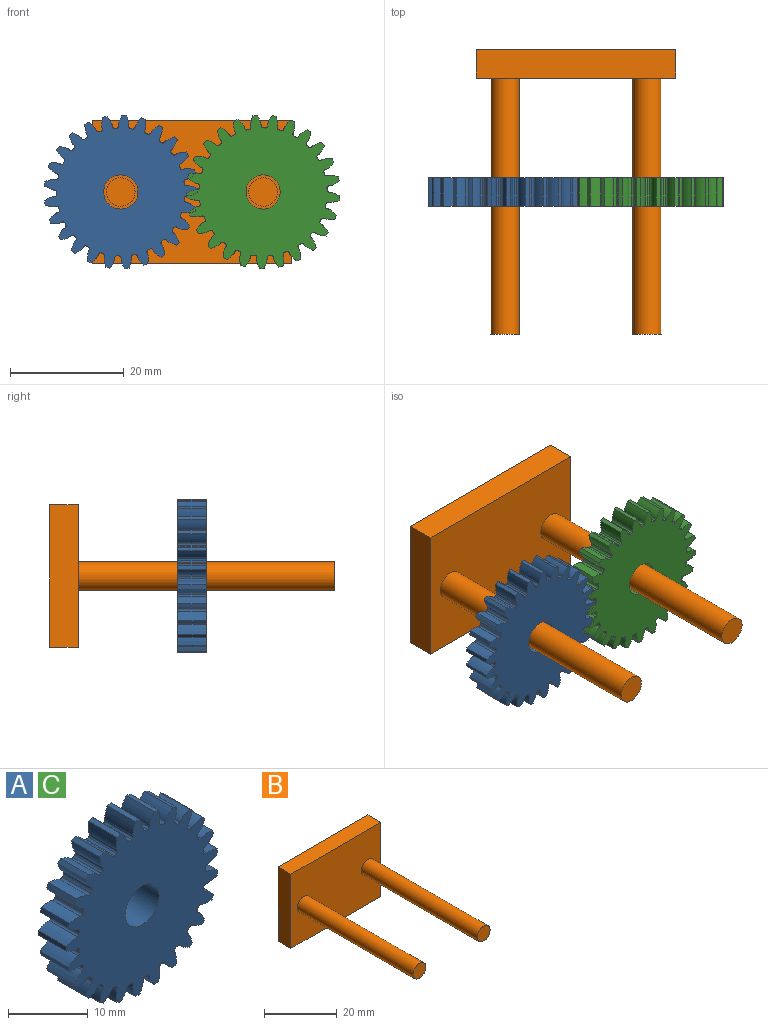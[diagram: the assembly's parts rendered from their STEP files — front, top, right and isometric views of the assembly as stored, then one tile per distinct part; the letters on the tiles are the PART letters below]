
ASSEMBLY  parts=3 mates=2
PART A: 153 faces, bbox 26.9x5x27 mm
  f0: extruded ~5x1.84mm, area 10.1mm2, adj f100,f101,f102,f103
  f1: cylinder r=11.25mm len=5mm, axis (0,1,0), area 1.9mm2, adj f101,f102,f103,f104
  f2: extruded ~5x1.84mm, area 10.1mm2, adj f3,f101,f102,f104
  f3: cylinder r=13.5mm len=5mm, axis (0,1,0), area 3.6mm2, adj f2,f4,f101,f102
  f4: extruded ~5x1.98mm, area 10.1mm2, adj f3,f101,f102,f105
  f5: cylinder r=11.25mm len=5mm, axis (0,1,0), area 1.9mm2, adj f101,f102,f105,f106
  f6: extruded ~5x1.59mm, area 10.1mm2, adj f7,f101,f102,f106
  f7: cylinder r=13.5mm len=5mm, axis (0,1,0), area 3.6mm2, adj f6,f8,f101,f102
  f8: extruded ~5x1.99mm, area 10.1mm2, adj f7,f101,f102,f107
  f9: cylinder r=11.25mm len=5mm, axis (0,1,0), area 1.9mm2, adj f101,f102,f107,f108
  f10: extruded ~5x1.57mm, area 10.1mm2, adj f11,f101,f102,f108
  f11: cylinder r=13.5mm len=5mm, axis (0,1,0), area 3.6mm2, adj f10,f12,f101,f102
  f12: extruded ~5x1.88mm, area 10.1mm2, adj f11,f101,f102,f109
  f13: cylinder r=11.25mm len=5mm, axis (0,1,0), area 1.9mm2, adj f101,f102,f109,f110
  f14: extruded ~5x1.83mm, area 10.1mm2, adj f15,f101,f102,f110
  f15: cylinder r=13.5mm len=5mm, axis (0,1,0), area 3.6mm2, adj f14,f16,f101,f102
  f16: extruded ~5x1.65mm, area 10.1mm2, adj f15,f101,f102,f111
  f17: cylinder r=11.25mm len=5mm, axis (0,1,0), area 1.9mm2, adj f101,f102,f111,f112
  f18: extruded ~5x1.97mm, area 10.1mm2, adj f19,f101,f102,f112
  f19: cylinder r=13.5mm len=5mm, axis (0,1,0), area 3.6mm2, adj f18,f20,f101,f102
  f20: extruded ~5x1.51mm, area 10.1mm2, adj f19,f101,f102,f113
  f21: cylinder r=11.25mm len=5mm, axis (0,1,0), area 1.9mm2, adj f101,f102,f113,f114
  f22: extruded ~5x1.99mm, area 10.1mm2, adj f23,f101,f102,f114
  f23: cylinder r=13.5mm len=5mm, axis (0,1,0), area 3.6mm2, adj f22,f24,f101,f102
  f24: extruded ~5x1.79mm, area 10.1mm2, adj f23,f101,f102,f115
  f25: cylinder r=11.25mm len=5mm, axis (0,1,0), area 1.9mm2, adj f101,f102,f115,f116
  f26: extruded ~5x1.89mm, area 10.1mm2, adj f27,f101,f102,f116
  f27: cylinder r=13.5mm len=5mm, axis (0,1,0), area 3.6mm2, adj f26,f28,f101,f102
  f28: extruded ~5x1.96mm, area 10.1mm2, adj f27,f101,f102,f117
  f29: cylinder r=11.25mm len=5mm, axis (0,1,0), area 1.9mm2, adj f101,f102,f117,f118
  f30: extruded ~5x1.67mm, area 10.1mm2, adj f31,f101,f102,f118
  f31: cylinder r=13.5mm len=5mm, axis (0,1,0), area 3.6mm2, adj f30,f32,f101,f102
  f32: extruded ~5x2mm, area 10.1mm2, adj f31,f101,f102,f119
  f33: cylinder r=11.25mm len=5mm, axis (0,1,0), area 1.9mm2, adj f101,f102,f119,f120
  f34: extruded ~5x1.49mm, area 10.1mm2, adj f35,f101,f102,f120
  f35: cylinder r=13.5mm len=5mm, axis (0,1,0), area 3.6mm2, adj f34,f36,f101,f102
  f36: extruded ~5x1.92mm, area 10.1mm2, adj f35,f101,f102,f121
  f37: cylinder r=11.25mm len=5mm, axis (0,1,0), area 1.9mm2, adj f101,f102,f121,f122
  f38: extruded ~5x1.78mm, area 10.1mm2, adj f39,f101,f102,f122
  f39: cylinder r=13.5mm len=5mm, axis (0,1,0), area 3.6mm2, adj f38,f40,f101,f102
  f40: extruded ~5x1.72mm, area 10.1mm2, adj f39,f101,f102,f123
  f41: cylinder r=11.25mm len=5mm, axis (0,1,0), area 1.9mm2, adj f101,f102,f123,f124
  f42: extruded ~5x1.95mm, area 10.1mm2, adj f43,f101,f102,f124
  f43: cylinder r=13.5mm len=5mm, axis (0,1,0), area 3.6mm2, adj f42,f44,f101,f102
  f44: extruded ~5x1.43mm, area 10.1mm2, adj f43,f101,f102,f125
  f45: cylinder r=11.25mm len=5mm, axis (0,1,0), area 1.9mm2, adj f101,f102,f125,f126
  f46: extruded ~5x2mm, area 10.1mm2, adj f47,f101,f102,f126
  f47: cylinder r=13.5mm len=5mm, axis (0,1,0), area 3.6mm2, adj f46,f48,f101,f102
  f48: extruded ~5x1.73mm, area 10.1mm2, adj f47,f101,f102,f127
  f49: cylinder r=11.25mm len=5mm, axis (0,1,0), area 1.9mm2, adj f101,f102,f127,f128
  f50: extruded ~5x1.93mm, area 10.1mm2, adj f51,f101,f102,f128
  f51: cylinder r=13.5mm len=5mm, axis (0,1,0), area 3.6mm2, adj f50,f52,f101,f102
  f52: extruded ~5x1.93mm, area 10.1mm2, adj f51,f101,f102,f129
  f53: cylinder r=11.25mm len=5mm, axis (0,1,0), area 1.9mm2, adj f101,f102,f129,f130
  f54: extruded ~5x1.73mm, area 10.1mm2, adj f55,f101,f102,f130
  f55: cylinder r=13.5mm len=5mm, axis (0,1,0), area 3.6mm2, adj f54,f56,f101,f102
  f56: extruded ~5x2mm, area 10.1mm2, adj f55,f101,f102,f131
  f57: cylinder r=11.25mm len=5mm, axis (0,1,0), area 1.9mm2, adj f101,f102,f131,f132
  f58: extruded ~5x1.43mm, area 10.1mm2, adj f59,f101,f102,f132
  f59: cylinder r=13.5mm len=5mm, axis (0,1,0), area 3.6mm2, adj f58,f60,f101,f102
  f60: extruded ~5x1.95mm, area 10.1mm2, adj f59,f101,f102,f133
  f61: cylinder r=11.25mm len=5mm, axis (0,1,0), area 1.9mm2, adj f101,f102,f133,f134
  f62: extruded ~5x1.72mm, area 10.1mm2, adj f63,f101,f102,f134
  f63: cylinder r=13.5mm len=5mm, axis (0,1,0), area 3.6mm2, adj f62,f64,f101,f102
  f64: extruded ~5x1.78mm, area 10.1mm2, adj f63,f101,f102,f135
  f65: cylinder r=11.25mm len=5mm, axis (0,1,0), area 1.9mm2, adj f101,f102,f135,f136
  f66: extruded ~5x1.92mm, area 10.1mm2, adj f67,f101,f102,f136
  f67: cylinder r=13.5mm len=5mm, axis (0,1,0), area 3.6mm2, adj f66,f68,f101,f102
  f68: extruded ~5x1.49mm, area 10.1mm2, adj f67,f101,f102,f137
  f69: cylinder r=11.25mm len=5mm, axis (0,1,0), area 1.9mm2, adj f101,f102,f137,f138
  f70: extruded ~5x2mm, area 10.1mm2, adj f71,f101,f102,f138
  f71: cylinder r=13.5mm len=5mm, axis (0,1,0), area 3.6mm2, adj f70,f72,f101,f102
  f72: extruded ~5x1.67mm, area 10.1mm2, adj f71,f101,f102,f139
  f73: cylinder r=11.25mm len=5mm, axis (0,1,0), area 1.9mm2, adj f101,f102,f139,f140
  f74: extruded ~5x1.96mm, area 10.1mm2, adj f75,f101,f102,f140
  f75: cylinder r=13.5mm len=5mm, axis (0,1,0), area 3.6mm2, adj f74,f76,f101,f102
  f76: extruded ~5x1.89mm, area 10.1mm2, adj f75,f101,f102,f141
  f77: cylinder r=11.25mm len=5mm, axis (0,1,0), area 1.9mm2, adj f101,f102,f141,f142
  f78: extruded ~5x1.79mm, area 10.1mm2, adj f79,f101,f102,f142
  f79: cylinder r=13.5mm len=5mm, axis (0,1,0), area 3.6mm2, adj f78,f80,f101,f102
  f80: extruded ~5x1.99mm, area 10.1mm2, adj f79,f101,f102,f143
  f81: cylinder r=11.25mm len=5mm, axis (0,1,0), area 1.9mm2, adj f101,f102,f143,f144
  f82: extruded ~5x1.51mm, area 10.1mm2, adj f83,f101,f102,f144
  f83: cylinder r=13.5mm len=5mm, axis (0,1,0), area 3.6mm2, adj f82,f84,f101,f102
  f84: extruded ~5x1.97mm, area 10.1mm2, adj f83,f101,f102,f145
  f85: cylinder r=11.25mm len=5mm, axis (0,1,0), area 1.9mm2, adj f101,f102,f145,f146
  f86: extruded ~5x1.65mm, area 10.1mm2, adj f87,f101,f102,f146
  f87: cylinder r=13.5mm len=5mm, axis (0,1,0), area 3.6mm2, adj f86,f88,f101,f102
  f88: extruded ~5x1.83mm, area 10.1mm2, adj f87,f101,f102,f147
  f89: cylinder r=11.25mm len=5mm, axis (0,1,0), area 1.9mm2, adj f101,f102,f147,f148
  f90: extruded ~5x1.88mm, area 10.1mm2, adj f91,f101,f102,f148
  f91: cylinder r=13.5mm len=5mm, axis (0,1,0), area 3.6mm2, adj f90,f92,f101,f102
  f92: extruded ~5x1.57mm, area 10.1mm2, adj f91,f101,f102,f149
  f93: cylinder r=11.25mm len=5mm, axis (0,1,0), area 1.9mm2, adj f101,f102,f149,f150
  f94: extruded ~5x1.99mm, area 10.1mm2, adj f95,f101,f102,f150
  f95: cylinder r=13.5mm len=5mm, axis (0,1,0), area 3.6mm2, adj f94,f96,f101,f102
  f96: extruded ~5x1.59mm, area 10.1mm2, adj f95,f101,f102,f151
  f97: cylinder r=11.25mm len=5mm, axis (0,1,0), area 1.9mm2, adj f101,f102,f151,f152
  f98: extruded ~5x1.98mm, area 10.1mm2, adj f100,f101,f102,f152
  f99: cylinder r=3mm len=6mm, axis (0,1,0), area 94.2mm2, adj f101,f102
  f100: cylinder r=13.5mm len=5mm, axis (0,1,0), area 3.6mm2, adj f0,f98,f101,f102
  f101: plane 26.99x26.94mm, normal (0,-1,0), area 455.2mm2, adj f0,f1,f2,f3,f4,f5,f6,f7
  f102: plane 26.99x26.94mm, normal (0,1,0), area 455.2mm2, adj f0,f1,f2,f3,f4,f5,f6,f7
  f103: cylinder r=0.36mm len=5mm, axis (0,1,0), area 2.8mm2, adj f0,f1,f101,f102
  f104: cylinder r=0.36mm len=5mm, axis (0,1,0), area 2.8mm2, adj f1,f2,f101,f102
  f105: cylinder r=0.36mm len=5mm, axis (0,1,0), area 2.8mm2, adj f4,f5,f101,f102
  f106: cylinder r=0.36mm len=5mm, axis (0,1,0), area 2.8mm2, adj f5,f6,f101,f102
  f107: cylinder r=0.36mm len=5mm, axis (0,1,0), area 2.8mm2, adj f8,f9,f101,f102
  f108: cylinder r=0.36mm len=5mm, axis (0,1,0), area 2.8mm2, adj f9,f10,f101,f102
  f109: cylinder r=0.36mm len=5mm, axis (0,1,0), area 2.8mm2, adj f12,f13,f101,f102
  f110: cylinder r=0.36mm len=5mm, axis (0,1,0), area 2.8mm2, adj f13,f14,f101,f102
  f111: cylinder r=0.36mm len=5mm, axis (0,1,0), area 2.8mm2, adj f16,f17,f101,f102
  f112: cylinder r=0.36mm len=5mm, axis (0,1,0), area 2.8mm2, adj f17,f18,f101,f102
  f113: cylinder r=0.36mm len=5mm, axis (0,1,0), area 2.8mm2, adj f20,f21,f101,f102
  f114: cylinder r=0.36mm len=5mm, axis (0,1,0), area 2.8mm2, adj f21,f22,f101,f102
  f115: cylinder r=0.36mm len=5mm, axis (0,1,0), area 2.8mm2, adj f24,f25,f101,f102
  f116: cylinder r=0.36mm len=5mm, axis (0,1,0), area 2.8mm2, adj f25,f26,f101,f102
  f117: cylinder r=0.36mm len=5mm, axis (0,1,0), area 2.8mm2, adj f28,f29,f101,f102
  f118: cylinder r=0.36mm len=5mm, axis (0,1,0), area 2.8mm2, adj f29,f30,f101,f102
  f119: cylinder r=0.36mm len=5mm, axis (0,1,0), area 2.8mm2, adj f32,f33,f101,f102
  f120: cylinder r=0.36mm len=5mm, axis (0,1,0), area 2.8mm2, adj f33,f34,f101,f102
  f121: cylinder r=0.36mm len=5mm, axis (0,1,0), area 2.8mm2, adj f36,f37,f101,f102
  f122: cylinder r=0.36mm len=5mm, axis (0,1,0), area 2.8mm2, adj f37,f38,f101,f102
  f123: cylinder r=0.36mm len=5mm, axis (0,1,0), area 2.8mm2, adj f40,f41,f101,f102
  f124: cylinder r=0.36mm len=5mm, axis (0,1,0), area 2.8mm2, adj f41,f42,f101,f102
  f125: cylinder r=0.36mm len=5mm, axis (0,1,0), area 2.8mm2, adj f44,f45,f101,f102
  f126: cylinder r=0.36mm len=5mm, axis (0,1,0), area 2.8mm2, adj f45,f46,f101,f102
  f127: cylinder r=0.36mm len=5mm, axis (0,1,0), area 2.8mm2, adj f48,f49,f101,f102
  f128: cylinder r=0.36mm len=5mm, axis (0,1,0), area 2.8mm2, adj f49,f50,f101,f102
  f129: cylinder r=0.36mm len=5mm, axis (0,1,0), area 2.8mm2, adj f52,f53,f101,f102
  f130: cylinder r=0.36mm len=5mm, axis (0,1,0), area 2.8mm2, adj f53,f54,f101,f102
  f131: cylinder r=0.36mm len=5mm, axis (0,1,0), area 2.8mm2, adj f56,f57,f101,f102
  f132: cylinder r=0.36mm len=5mm, axis (0,1,0), area 2.8mm2, adj f57,f58,f101,f102
  f133: cylinder r=0.36mm len=5mm, axis (0,1,0), area 2.8mm2, adj f60,f61,f101,f102
  f134: cylinder r=0.36mm len=5mm, axis (0,1,0), area 2.8mm2, adj f61,f62,f101,f102
  f135: cylinder r=0.36mm len=5mm, axis (0,1,0), area 2.8mm2, adj f64,f65,f101,f102
  f136: cylinder r=0.36mm len=5mm, axis (0,1,0), area 2.8mm2, adj f65,f66,f101,f102
  f137: cylinder r=0.36mm len=5mm, axis (0,1,0), area 2.8mm2, adj f68,f69,f101,f102
  f138: cylinder r=0.36mm len=5mm, axis (0,1,0), area 2.8mm2, adj f69,f70,f101,f102
  f139: cylinder r=0.36mm len=5mm, axis (0,1,0), area 2.8mm2, adj f72,f73,f101,f102
  f140: cylinder r=0.36mm len=5mm, axis (0,1,0), area 2.8mm2, adj f73,f74,f101,f102
  f141: cylinder r=0.36mm len=5mm, axis (0,1,0), area 2.8mm2, adj f76,f77,f101,f102
  f142: cylinder r=0.36mm len=5mm, axis (0,1,0), area 2.8mm2, adj f77,f78,f101,f102
  f143: cylinder r=0.36mm len=5mm, axis (0,1,0), area 2.8mm2, adj f80,f81,f101,f102
  f144: cylinder r=0.36mm len=5mm, axis (0,1,0), area 2.8mm2, adj f81,f82,f101,f102
  f145: cylinder r=0.36mm len=5mm, axis (0,1,0), area 2.8mm2, adj f84,f85,f101,f102
  f146: cylinder r=0.36mm len=5mm, axis (0,1,0), area 2.8mm2, adj f85,f86,f101,f102
  f147: cylinder r=0.36mm len=5mm, axis (0,1,0), area 2.8mm2, adj f88,f89,f101,f102
  f148: cylinder r=0.36mm len=5mm, axis (0,1,0), area 2.8mm2, adj f89,f90,f101,f102
  f149: cylinder r=0.36mm len=5mm, axis (0,1,0), area 2.8mm2, adj f92,f93,f101,f102
  f150: cylinder r=0.36mm len=5mm, axis (0,1,0), area 2.8mm2, adj f93,f94,f101,f102
  f151: cylinder r=0.36mm len=5mm, axis (0,1,0), area 2.8mm2, adj f96,f97,f101,f102
  f152: cylinder r=0.36mm len=5mm, axis (0,1,0), area 2.8mm2, adj f97,f98,f101,f102
PART B: 10 faces, bbox 35x50x25 mm
  f0: plane 25x5mm, normal (1,0,0), area 125mm2, adj f1,f3,f4,f5
  f1: plane 35x5mm, normal (0,0,1), area 175mm2, adj f0,f2,f4,f5
  f2: plane 25x5mm, normal (-1,0,0), area 125mm2, adj f1,f3,f4,f5
  f3: plane 35x5mm, normal (0,0,-1), area 175mm2, adj f0,f2,f4,f5
  f4: plane 35x25mm, normal (0,-1,0), area 835.7mm2, adj f0,f1,f2,f3,f6,f8
  f5: plane 35x25mm, normal (0,1,0), area 875mm2, adj f0,f1,f2,f3
  f6: cylinder r=2.5mm len=45mm, axis (0,1,0), area 706.9mm2, adj f4,f7
  f7: plane 5x5mm, normal (0,-1,0), area 19.6mm2, adj f6
  f8: cylinder r=2.5mm len=45mm, axis (0,1,0), area 706.9mm2, adj f4,f9
  f9: plane 5x5mm, normal (0,-1,0), area 19.6mm2, adj f8
PART C: same geometry as A
PLACE A rot(axis=(0,-1,0),109deg) t=(-13.52,-10.51,21.25)mm
PLACE B t=(-37.01,11.99,21.25)mm fixed
PLACE C rot(axis=(0,-1,0),161deg) t=(11.48,-10.51,21.25)mm
MATE revolute B.f8 <-> C.f3  axis (0,1,0) through (11.48,-15.51,21.25)mm
MATE revolute B.f6 <-> A.f3  axis (0,1,0) through (-13.52,-15.51,21.25)mm
